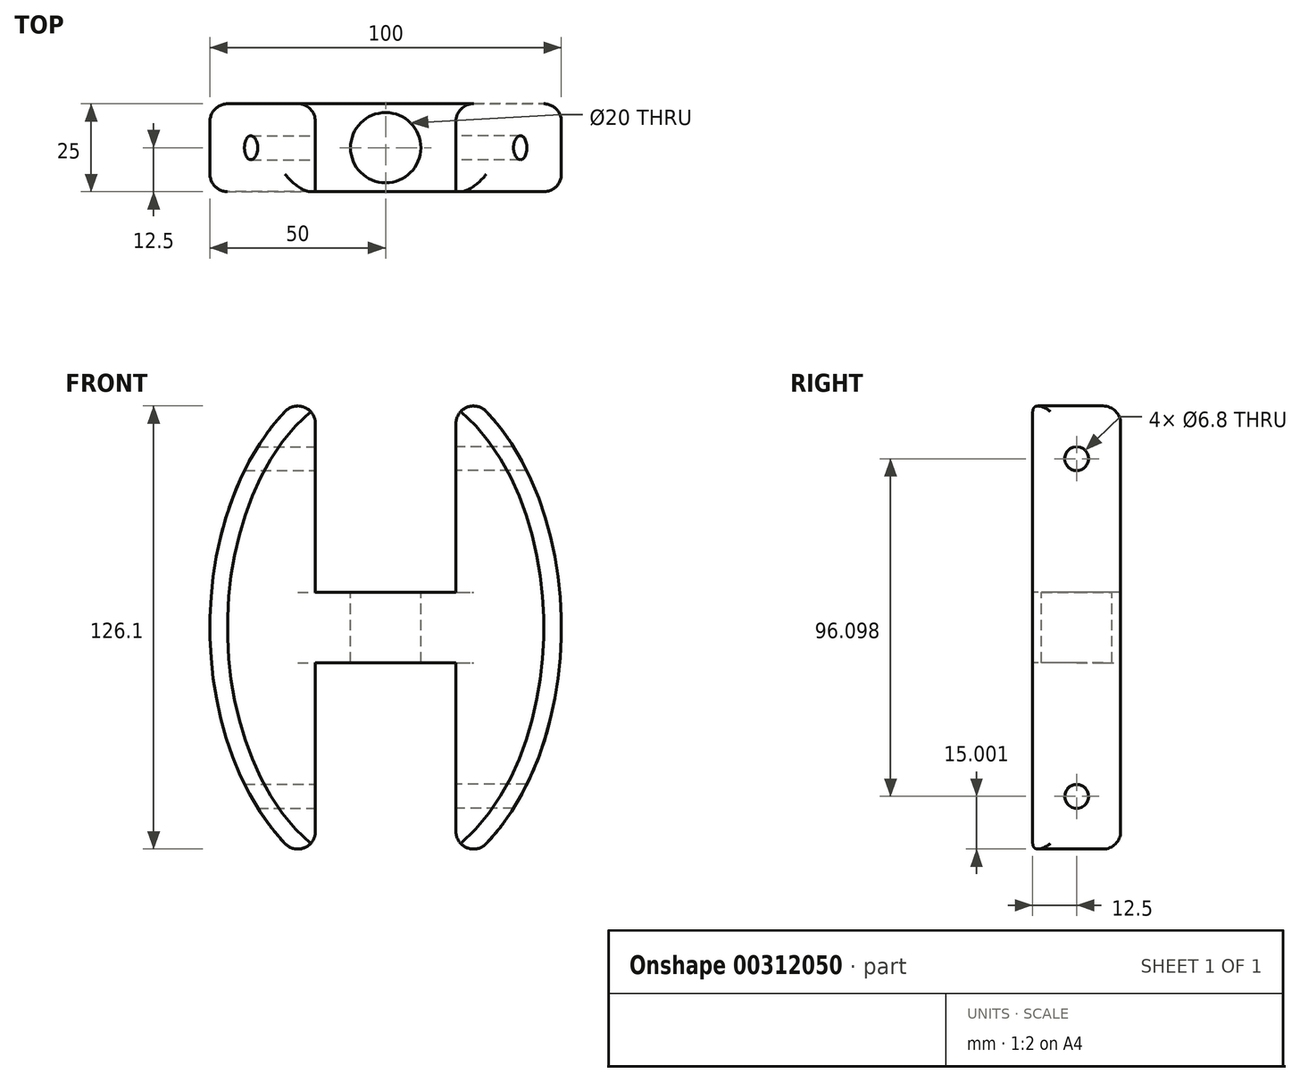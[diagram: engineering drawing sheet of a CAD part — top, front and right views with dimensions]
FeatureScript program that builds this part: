
annotation { "Feature Type Name" : "Feature", "Feature Type Description" : "" }
export const myFeature = defineFeature(function(context is Context, id is Id, definition is map)
    precondition{}
    {
        {
            var Q0;
            Q0=qCreatedBy(makeId("Front.planeOp"),FACE);
            var sketch = newSketch(context, id + "F0", { "sketchPlane" : qUnion([Q0])});
            skEllipse(sketch, "E0", {"center": v(0, 0) * mm, "majorRadius": 75 * mm, "minorRadius": 50 * mm, "majorAxis": v(0, 1)});
            skSolve(sketch);
        }
        {
            var Q0;
            Q0 = qSketchRegion(id + "F0", true);
            extrude(context, id + "F1", {"entities" : qUnion([Q0]), "depth" : 25 * mm});
        }
        {
            var Q0;
            Q0=makeQuery(id+"F1.opExtrude","CAP_FACE",FACE,{"disambiguationData":[OSD([sQuery(id+"F0.wireOp",EDGE,"E0")])],"isStart":false});
            var sketch = newSketch(context, id + "F2", { "sketchPlane" : qUnion([Q0])});
            skLineSegment(sketch, "E1.bottom", {"start": v(-68.83, 10) * mm, "end": v(68.83, 10) * mm, "construction": true});
            skLineSegment(sketch, "E1.top", {"start": v(-68.83, -10) * mm, "end": v(68.83, -10) * mm, "construction": true});
            skLineSegment(sketch, "E1.left", {"start": v(-68.83, 10) * mm, "end": v(-68.83, -10) * mm, "construction": true});
            skLineSegment(sketch, "E1.right", {"start": v(68.83, 10) * mm, "end": v(68.83, -10) * mm, "construction": true});
            skPoint(sketch, "E1.middle", {"position": v(0, 0) * mm});
            skLineSegment(sketch, "E2", {"start": v(0, 101.6) * mm, "end": v(0, -106.96) * mm, "construction": true});
            skPoint(sketch, "E2.endSnap0", {"position": v(0, 75) * mm});
            skLineSegment(sketch, "E3.bottom", {"start": v(-20, -10) * mm, "end": v(20, -10) * mm});
            skLineSegment(sketch, "E3.top", {"start": v(-20, -140) * mm, "end": v(20, -140) * mm});
            skLineSegment(sketch, "E3.left", {"start": v(-20, -10) * mm, "end": v(-20, -140) * mm});
            skLineSegment(sketch, "E3.right", {"start": v(20, -10) * mm, "end": v(20, -140) * mm});
            skPoint(sketch, "E3.middle", {"position": v(0, -75) * mm});
            skLineSegment(sketch, "E4.bottom", {"start": v(-20, 10) * mm, "end": v(20, 10) * mm});
            skLineSegment(sketch, "E4.top", {"start": v(-20, 140) * mm, "end": v(20, 140) * mm});
            skLineSegment(sketch, "E4.left", {"start": v(-20, 10) * mm, "end": v(-20, 140) * mm});
            skLineSegment(sketch, "E4.right", {"start": v(20, 10) * mm, "end": v(20, 140) * mm});
            skSolve(sketch);
        }
        {
            var Q0;
            Q0 = qSketchRegion(id + "F2", true);
            extrude(context, id + "F3", {"entities" : qUnion([Q0]), "operationType" : NewBodyOperationType.REMOVE, "endBound" : BoundingType.THROUGH_ALL, "oppositeDirection" : true, "depth" : 25 * mm});
        }
        {
            var Q0;
            {var subQ0=sQuery(id+"F0.wireOp",EDGE,"E0");Q0=makeQuery(id+"F3.boolean.opBoolean","SPLIT",EDGE,{"disambiguationData":[TD([makeQuery(id+"F3.opExtrude","SWEPT_FACE",FACE,{"disambiguationData":[OSD([sQuery(id+"F2.wireOp",EDGE,"E3.left")])]})])],"derivedFrom":makeQuery(id+"F1.opExtrude","CAP_EDGE",EDGE,{"disambiguationData":[OSD([subQ0])],"isStart":false})});}
            var Q1;
            {var subQ0=sQuery(id+"F0.wireOp",EDGE,"E0");Q1=makeQuery(id+"F3.boolean.opBoolean","SPLIT",EDGE,{"disambiguationData":[TD([makeQuery(id+"F3.opExtrude","SWEPT_FACE",FACE,{"disambiguationData":[OSD([sQuery(id+"F2.wireOp",EDGE,"E3.right")])]})])],"derivedFrom":makeQuery(id+"F1.opExtrude","CAP_EDGE",EDGE,{"disambiguationData":[OSD([subQ0])],"isStart":true})});}
            var Q2;
            {var subQ0=sQuery(id+"F0.wireOp",EDGE,"E0");Q2=makeQuery(id+"F3.boolean.opBoolean","SPLIT",EDGE,{"disambiguationData":[TD([makeQuery(id+"F3.opExtrude","SWEPT_FACE",FACE,{"disambiguationData":[OSD([sQuery(id+"F2.wireOp",EDGE,"E3.right")])]})])],"derivedFrom":makeQuery(id+"F1.opExtrude","CAP_EDGE",EDGE,{"disambiguationData":[OSD([subQ0])],"isStart":false})});}
            var Q3;
            {var subQ0=sQuery(id+"F0.wireOp",EDGE,"E0");Q3=makeQuery(id+"F3.boolean.opBoolean","SPLIT",EDGE,{"disambiguationData":[TD([makeQuery(id+"F3.opExtrude","SWEPT_FACE",FACE,{"disambiguationData":[OSD([sQuery(id+"F2.wireOp",EDGE,"E3.left")])]})])],"derivedFrom":makeQuery(id+"F1.opExtrude","CAP_EDGE",EDGE,{"disambiguationData":[OSD([subQ0])],"isStart":true})});}
            var Q4;
            Q4=makeQuery(id+"F3.boolean.opBoolean","INTERSECT",EDGE,{"derivedFrom":[makeQuery(id+"F1.opExtrude","CAP_FACE",FACE,{"disambiguationData":[OSD([sQuery(id+"F0.wireOp",EDGE,"E0")])],"isStart":true}),makeQuery(id+"F3.opExtrude","SWEPT_FACE",FACE,{"disambiguationData":[OSD([sQuery(id+"F2.wireOp",EDGE,"E3.left")])]})]});
            var Q5;
            Q5=makeQuery(id+"F3.boolean.opBoolean","INTERSECT",EDGE,{"derivedFrom":[makeQuery(id+"F1.opExtrude","CAP_FACE",FACE,{"disambiguationData":[OSD([sQuery(id+"F0.wireOp",EDGE,"E0")])],"isStart":true}),makeQuery(id+"F3.opExtrude","SWEPT_FACE",FACE,{"disambiguationData":[OSD([sQuery(id+"F2.wireOp",EDGE,"E3.right")])]})]});
            var Q6;
            Q6=makeQuery(id+"F3.boolean.opBoolean","INTERSECT",EDGE,{"derivedFrom":[makeQuery(id+"F1.opExtrude","CAP_FACE",FACE,{"disambiguationData":[OSD([sQuery(id+"F0.wireOp",EDGE,"E0")])],"isStart":true}),makeQuery(id+"F3.opExtrude","SWEPT_FACE",FACE,{"disambiguationData":[OSD([sQuery(id+"F2.wireOp",EDGE,"E4.right")])]})]});
            var Q7;
            Q7=makeQuery(id+"F3.boolean.opBoolean","INTERSECT",EDGE,{"derivedFrom":[makeQuery(id+"F1.opExtrude","CAP_FACE",FACE,{"disambiguationData":[OSD([sQuery(id+"F0.wireOp",EDGE,"E0")])],"isStart":true}),makeQuery(id+"F3.opExtrude","SWEPT_FACE",FACE,{"disambiguationData":[OSD([sQuery(id+"F2.wireOp",EDGE,"E4.left")])]})]});
            var Q8;
            Q8=makeQuery(id+"F3.boolean.opBoolean","COPY",EDGE,{"derivedFrom":makeQuery(id+"F3.opExtrude","CAP_EDGE",EDGE,{"disambiguationData":[OSD([sQuery(id+"F2.wireOp",EDGE,"E4.left")])],"isStart":true})});
            var Q9;
            Q9=makeQuery(id+"F3.boolean.opBoolean","COPY",EDGE,{"derivedFrom":makeQuery(id+"F3.opExtrude","CAP_EDGE",EDGE,{"disambiguationData":[OSD([sQuery(id+"F2.wireOp",EDGE,"E4.right")])],"isStart":true})});
            var Q10;
            Q10=makeQuery(id+"F3.boolean.opBoolean","COPY",EDGE,{"derivedFrom":makeQuery(id+"F3.opExtrude","CAP_EDGE",EDGE,{"disambiguationData":[OSD([sQuery(id+"F2.wireOp",EDGE,"E3.left")])],"isStart":true})});
            var Q11;
            Q11=makeQuery(id+"F3.boolean.opBoolean","COPY",EDGE,{"derivedFrom":makeQuery(id+"F3.opExtrude","CAP_EDGE",EDGE,{"disambiguationData":[OSD([sQuery(id+"F2.wireOp",EDGE,"E3.right")])],"isStart":true})});
            var Q12;
            Q12=makeQuery(id+"F3.boolean.opBoolean","INTERSECT",EDGE,{"derivedFrom":[makeQuery(id+"F1.opExtrude","SWEPT_FACE",FACE,{"disambiguationData":[OSD([sQuery(id+"F0.wireOp",EDGE,"E0")])]}),makeQuery(id+"F3.opExtrude","SWEPT_FACE",FACE,{"disambiguationData":[OSD([sQuery(id+"F2.wireOp",EDGE,"E4.left")])]})]});
            var Q13;
            Q13=makeQuery(id+"F3.boolean.opBoolean","INTERSECT",EDGE,{"derivedFrom":[makeQuery(id+"F1.opExtrude","SWEPT_FACE",FACE,{"disambiguationData":[OSD([sQuery(id+"F0.wireOp",EDGE,"E0")])]}),makeQuery(id+"F3.opExtrude","SWEPT_FACE",FACE,{"disambiguationData":[OSD([sQuery(id+"F2.wireOp",EDGE,"E4.right")])]})]});
            var Q14;
            Q14=makeQuery(id+"F3.boolean.opBoolean","INTERSECT",EDGE,{"derivedFrom":[makeQuery(id+"F1.opExtrude","SWEPT_FACE",FACE,{"disambiguationData":[OSD([sQuery(id+"F0.wireOp",EDGE,"E0")])]}),makeQuery(id+"F3.opExtrude","SWEPT_FACE",FACE,{"disambiguationData":[OSD([sQuery(id+"F2.wireOp",EDGE,"E3.right")])]})]});
            var Q15;
            {var subQ0=sQuery(id+"F0.wireOp",EDGE,"E0");Q15=makeQuery(id+"F3.boolean.opBoolean","SPLIT",FACE,{"disambiguationData":[TD([makeQuery(id+"F3.opExtrude","SWEPT_FACE",FACE,{"disambiguationData":[OSD([sQuery(id+"F2.wireOp",EDGE,"E3.left")])]})])],"derivedFrom":makeQuery(id+"F1.opExtrude","SWEPT_FACE",FACE,{"disambiguationData":[OSD([subQ0])]})});}
            fillet(context, id + "F4", {"entities" : qUnion([Q0, Q1, Q2, Q3, Q4, Q5, Q6, Q7, Q8, Q9, Q10, Q11, Q12, Q13, Q14, Q15]), "radius" : 5 * mm, "tangentPropagation" : true, "allowEdgeOverflow" : false});
        }
        {
            var Q0;
            Q0=makeQuery(id+"F3.boolean.opBoolean","COPY",FACE,{"derivedFrom":makeQuery(id+"F3.opExtrude","SWEPT_FACE",FACE,{"disambiguationData":[OSD([sQuery(id+"F2.wireOp",EDGE,"E4.left")])]})});
            var sketch = newSketch(context, id + "F5", { "sketchPlane" : qUnion([Q0])});
            skLineSegment(sketch, "E5", {"start": v(-12.5, 58.05) * mm, "end": v(-12.5, 10) * mm, "construction": true});
            skLineSegment(sketch, "E6", {"start": v(-20, 48.05) * mm, "end": v(-5, 48.05) * mm, "construction": true});
            skPoint(sketch, "E7", {"position": v(-12.5, 48.05) * mm});
            skSolve(sketch);
        }
        {
            var Q0;
            Q0=makeQuery(id+"F3.boolean.opBoolean","COPY",FACE,{"derivedFrom":makeQuery(id+"F3.opExtrude","SWEPT_FACE",FACE,{"disambiguationData":[OSD([sQuery(id+"F2.wireOp",EDGE,"E4.right")])]})});
            var sketch = newSketch(context, id + "F6", { "sketchPlane" : qUnion([Q0])});
            skLineSegment(sketch, "E8", {"start": v(12.5, 58.05) * mm, "end": v(12.5, 10) * mm, "construction": true});
            skLineSegment(sketch, "E9", {"start": v(5, 48.05) * mm, "end": v(20, 48.05) * mm, "construction": true});
            skPoint(sketch, "E10", {"position": v(12.5, 48.05) * mm});
            skSolve(sketch);
        }
        {
            var Q0;
            Q0=makeQuery(id+"F3.boolean.opBoolean","COPY",FACE,{"derivedFrom":makeQuery(id+"F3.opExtrude","SWEPT_FACE",FACE,{"disambiguationData":[OSD([sQuery(id+"F2.wireOp",EDGE,"E3.left")])]})});
            var sketch = newSketch(context, id + "F7", { "sketchPlane" : qUnion([Q0])});
            skLineSegment(sketch, "E11", {"start": v(-12.5, -58.05) * mm, "end": v(-12.5, -10) * mm, "construction": true});
            skLineSegment(sketch, "E12", {"start": v(-5, -48.05) * mm, "end": v(-20, -48.05) * mm, "construction": true});
            skPoint(sketch, "E13", {"position": v(-12.5, -48.05) * mm});
            skSolve(sketch);
        }
        {
            var Q0;
            Q0=makeQuery(id+"F3.boolean.opBoolean","COPY",FACE,{"derivedFrom":makeQuery(id+"F3.opExtrude","SWEPT_FACE",FACE,{"disambiguationData":[OSD([sQuery(id+"F2.wireOp",EDGE,"E3.right")])]})});
            var sketch = newSketch(context, id + "F8", { "sketchPlane" : qUnion([Q0])});
            skLineSegment(sketch, "E14", {"start": v(12.5, -58.05) * mm, "end": v(12.5, -10) * mm, "construction": true});
            skLineSegment(sketch, "E15", {"start": v(20, -48.05) * mm, "end": v(5, -48.05) * mm, "construction": true});
            skPoint(sketch, "E16", {"position": v(12.5, -48.05) * mm});
            skSolve(sketch);
        }
        {
            var Q0;
            Q0=sQuery(id+"F5.wireOp",VERTEX,"E7");
            var Q1;
            Q1=sQuery(id+"F8.wireOp",VERTEX,"E16");
            var Q2;
            Q2=sQuery(id+"F7.wireOp",VERTEX,"E13");
            var Q3;
            Q3=sQuery(id+"F6.wireOp",VERTEX,"E10");
            var Q4;
            Q4=makeQuery(id+"F1.opExtrude","SWEPT_BODY",BODY,{"disambiguationData":[OSD([sQuery(id+"F0.wireOp",EDGE,"E0")])]});
            hole(context, id + "F9", {"style" : HoleStyle.SIMPLE, "endStyle" : HoleEndStyle.THROUGH, "standardTappedOrClearance" : lookupTablePath({ "standard" : "ISO", "engagement" : "75%", "pitch" : "1.25 mm", "size" : "M8", "type" : "Tapped" }), "standardBlindInLast" : lookupTablePath({ "standard" : "ISO", "engagement" : "75%", "pitch" : "1.25 mm", "size" : "M8", "type" : "Tapped" }), "holeDiameter" : 6.8 * mm, "showTappedDepth" : true, "tappedDepth" : 6 * mm, "tapClearance" : 3, "locations" : qUnion([Q0, Q1, Q2, Q3]), "scope" : qUnion([Q4]), "majorDiameter" : 8 * mm});
        }
        {
            var Q0;
            Q0=makeQuery(id+"F3.boolean.opBoolean","COPY",FACE,{"derivedFrom":makeQuery(id+"F3.opExtrude","SWEPT_FACE",FACE,{"disambiguationData":[OSD([sQuery(id+"F2.wireOp",EDGE,"E4.bottom")])]})});
            var sketch = newSketch(context, id + "F10", { "sketchPlane" : qUnion([Q0])});
            skLineSegment(sketch, "E17", {"start": v(20, -12.5) * mm, "end": v(-21.25, -12.5) * mm, "construction": true});
            skPoint(sketch, "E17.endSnap0", {"position": v(-20, -12.5) * mm});
            skLineSegment(sketch, "E18", {"start": v(0, 0) * mm, "end": v(0, -39.85) * mm, "construction": true});
            skPoint(sketch, "E19", {"position": v(0, -12.5) * mm});
            skCircle(sketch, "E20", {"center": v(0, -12.5) * mm, "radius": 10 * mm});
            skSolve(sketch);
        }
        {
            var Q0;
            Q0 = qSketchRegion(id + "F10", true);
            extrude(context, id + "F11", {"entities" : qUnion([Q0]), "operationType" : NewBodyOperationType.REMOVE, "endBound" : BoundingType.THROUGH_ALL, "oppositeDirection" : true, "depth" : 25 * mm});
        }
    });
